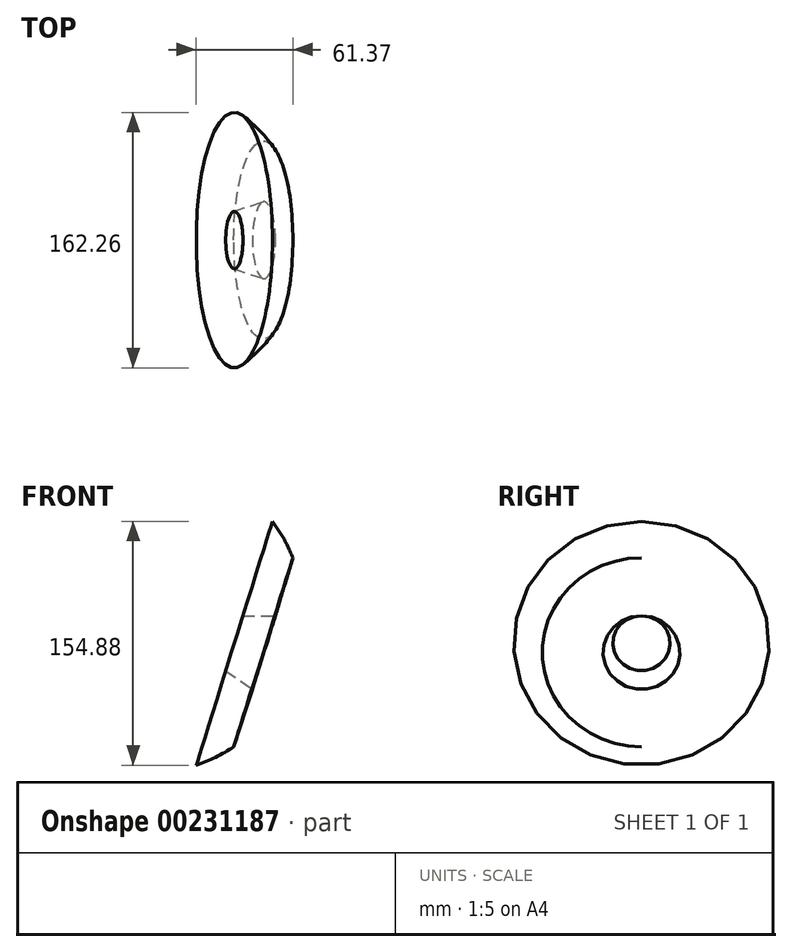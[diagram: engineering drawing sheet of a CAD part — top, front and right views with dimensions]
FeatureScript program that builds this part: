
annotation { "Feature Type Name" : "Feature", "Feature Type Description" : "" }
export const myFeature = defineFeature(function(context is Context, id is Id, definition is map)
    precondition{}
    {
        {
            var Q0;
            Q0=qCreatedBy(makeId("Front.planeOp"),FACE);
            var sketch = newSketch(context, id + "F0", { "sketchPlane" : qUnion([Q0])});
            skCircle(sketch, "E0", {"center": v(0, 0) * mm, "radius": 100 * mm});
            skLineSegment(sketch, "E1", {"start": v(0, 0) * mm, "end": v(0, -100) * mm});
            skLineSegment(sketch, "E2", {"start": v(0, 0) * mm, "end": v(0, 100) * mm});
            skLineSegment(sketch, "E3", {"start": v(0, -100) * mm, "end": v(30, -100) * mm});
            skLineSegment(sketch, "E4", {"start": v(0, -100) * mm, "end": v(-30, -100) * mm});
            skLineSegment(sketch, "E5", {"start": v(0, -100) * mm, "end": v(0, 60) * mm});
            skLineSegment(sketch, "E6", {"start": v(0, 60) * mm, "end": v(80, 60) * mm});
            skLineSegment(sketch, "E7", {"start": v(0, 60) * mm, "end": v(-80, 60) * mm});
            skLineSegment(sketch, "E8", {"start": v(-30, -100) * mm, "end": v(-80, 60) * mm});
            skLineSegment(sketch, "E9", {"start": v(30, -100) * mm, "end": v(80, 60) * mm});
            skLineSegment(sketch, "E10", {"start": v(-31.6, -94.88) * mm, "end": v(-80, 60) * mm});
            skLineSegment(sketch, "E11", {"start": v(31.6, -94.88) * mm, "end": v(80, 60) * mm});
            skLineSegment(sketch, "E12", {"start": v(-31.6, -94.88) * mm, "end": v(31.6, -94.88) * mm});
            skLineSegment(sketch, "E13", {"start": v(-55.8, -17.44) * mm, "end": v(-95.45, -29.83) * mm});
            skLineSegment(sketch, "E14", {"start": v(55.8, -17.44) * mm, "end": v(95.45, -29.83) * mm});
            skLineSegment(sketch, "E15", {"start": v(-55.8, -17.44) * mm, "end": v(-75.62, -23.63) * mm});
            skLineSegment(sketch, "E16", {"start": v(55.8, -17.44) * mm, "end": v(75.62, -23.63) * mm});
            skLineSegment(sketch, "E17", {"start": v(-30, -100) * mm, "end": v(-45, -100) * mm});
            skLineSegment(sketch, "E18", {"start": v(30, -100) * mm, "end": v(50, -100) * mm});
            skLineSegment(sketch, "E19", {"start": v(-55.8, -17.44) * mm, "end": v(-70.12, -21.91) * mm});
            skLineSegment(sketch, "E20", {"start": v(-45, -100) * mm, "end": v(-70.12, -21.91) * mm});
            skLineSegment(sketch, "E21", {"start": v(55.8, -17.44) * mm, "end": v(74.9, -23.4) * mm});
            skLineSegment(sketch, "E22", {"start": v(50, -100) * mm, "end": v(74.9, -23.4) * mm});
            skLineSegment(sketch, "E23", {"start": v(0, 0) * mm, "end": v(100, 0) * mm});
            skLineSegment(sketch, "E24", {"start": v(0, 0) * mm, "end": v(-100, 0) * mm});
            skSolve(sketch);
        }
        {
            var Q0;
            {var subQ5=sQuery(id+"F0.wireOp",EDGE,"E21");Q0=makeQuery(id+"F0.imprint","IMPRINT",FACE,{"disambiguationData":[TD([[makeQuery(id+"F0.imprint","IMPRINT",EDGE,{"derivedFrom":subQ5}),-1.0]])]});}
            var Q1;
            {var subQ0=sQuery(id+"F0.wireOp",EDGE,"E9");Q1=makeQuery(id+"F0.imprint","IMPRINT",FACE,{"disambiguationData":[TD([[makeQuery(id+"F0.imprint","IMPRINT",EDGE,{"derivedFrom":subQ0}),-1.0]])]});}
            var Q2;
            Q2=sQuery(id+"F0.wireOp",EDGE,"E16");
            revolve(context, id + "F1", {"entities" : qUnion([Q0, Q1]), "axis" : qUnion([Q2]), "revolveType" : RevolveType.FULL});
        }
        {
            var Q0;
            {var subQ5=sQuery(id+"F0.wireOp",EDGE,"E21");Q0=makeQuery(id+"F0.imprint","IMPRINT",FACE,{"disambiguationData":[TD([[makeQuery(id+"F0.imprint","IMPRINT",EDGE,{"derivedFrom":subQ5}),-1.0]])]});}
            var Q1;
            {var subQ0=sQuery(id+"F0.wireOp",EDGE,"E14");Q1=makeQuery(id+"F0.imprint","IMPRINT",FACE,{"disambiguationData":[TD([[makeQuery(id+"F0.imprint","IMPRINT",EDGE,{"derivedFrom":subQ0}),-1.0]])]});}
            var Q2;
            Q2=sQuery(id+"F0.wireOp",EDGE,"E14");
            revolve(context, id + "F2", {"operationType" : NewBodyOperationType.REMOVE, "entities" : qUnion([Q0, Q1]), "axis" : qUnion([Q2]), "revolveType" : RevolveType.FULL, "oppositeDirection" : true});
        }
    });
